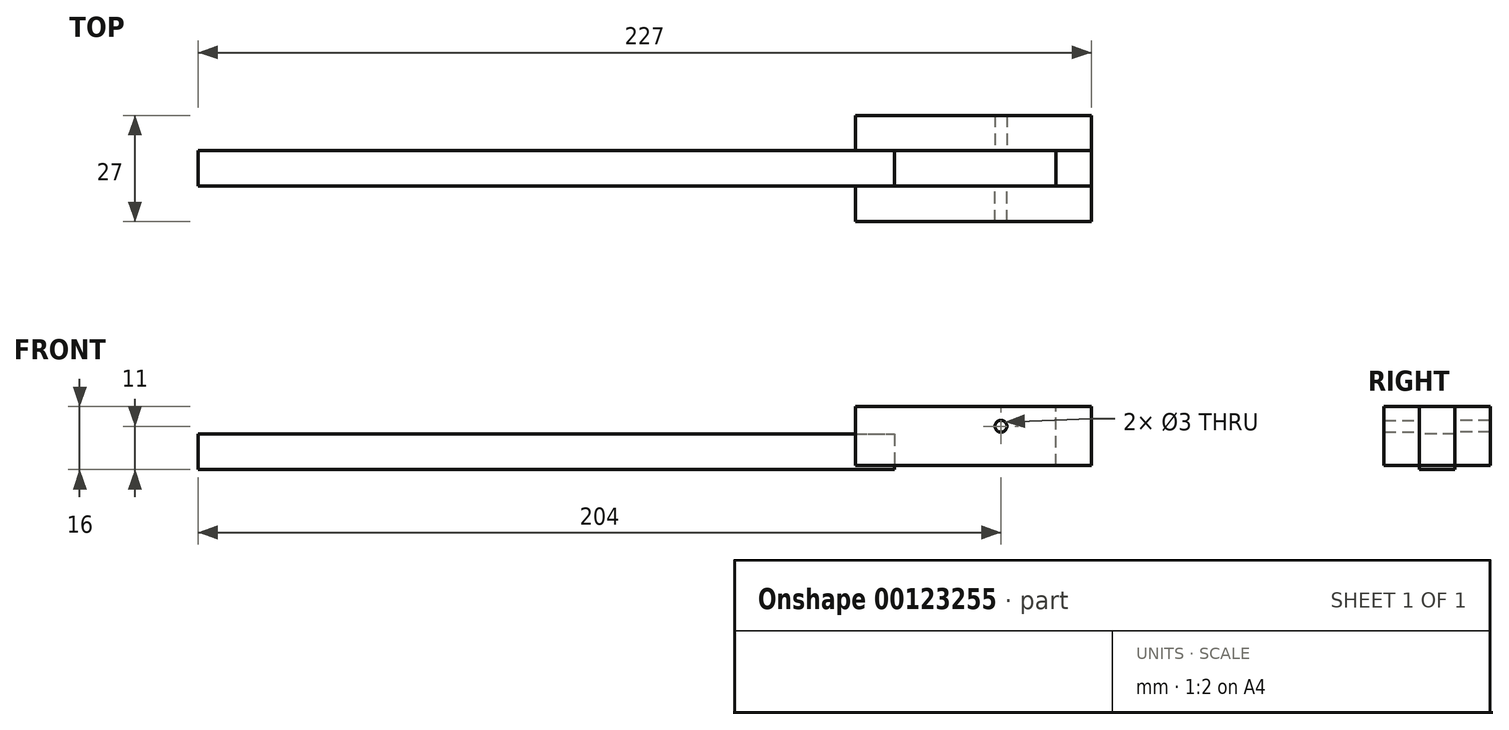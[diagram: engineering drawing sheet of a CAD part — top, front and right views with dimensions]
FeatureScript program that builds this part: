
annotation { "Feature Type Name" : "Feature", "Feature Type Description" : "" }
export const myFeature = defineFeature(function(context is Context, id is Id, definition is map)
    precondition{}
    {
        {
            var Q0;
            Q0=qCreatedBy(makeId("Front.planeOp"),FACE);
            var sketch = newSketch(context, id + "F0", { "sketchPlane" : qUnion([Q0])});
            skLineSegment(sketch, "E0.bottom", {"start": v(0, 9) * mm, "end": v(177, 9) * mm});
            skLineSegment(sketch, "E0.top", {"start": v(0, 0) * mm, "end": v(177, 0) * mm});
            skLineSegment(sketch, "E0.left", {"start": v(0, 9) * mm, "end": v(0, 0) * mm});
            skLineSegment(sketch, "E0.right", {"start": v(177, 9) * mm, "end": v(177, 0) * mm});
            skLineSegment(sketch, "E1.bottom", {"start": v(0, 0) * mm, "end": v(20, 0) * mm});
            skLineSegment(sketch, "E1.top", {"start": v(0, -30) * mm, "end": v(20, -30) * mm});
            skLineSegment(sketch, "E1.left", {"start": v(0, 0) * mm, "end": v(0, -30) * mm});
            skLineSegment(sketch, "E1.right", {"start": v(20, 0) * mm, "end": v(20, -30) * mm});
            skLineSegment(sketch, "E2.bottom", {"start": v(217.99, 1) * mm, "end": v(226.99, 1) * mm});
            skLineSegment(sketch, "E2.top", {"start": v(217.99, 16) * mm, "end": v(226.99, 16) * mm});
            skLineSegment(sketch, "E2.left", {"start": v(217.99, 1) * mm, "end": v(217.99, 16) * mm});
            skLineSegment(sketch, "E2.right", {"start": v(226.99, 1) * mm, "end": v(226.99, 16) * mm});
            skSolve(sketch);
        }
        {
            var Q0;
            Q0=makeQuery(id+"F0.imprint","IMPRINT",FACE,{"disambiguationData":[TD([[makeQuery(id+"F0.imprint","IMPRINT",EDGE,{"derivedFrom":sQuery(id+"F0.wireOp",EDGE,"E0.bottom")}),-1.0]])]});
            var Q1;
            Q1=makeQuery(id+"F0.imprint","IMPRINT",FACE,{"disambiguationData":[TD([[makeQuery(id+"F0.imprint","IMPRINT",EDGE,{"derivedFrom":sQuery(id+"F0.wireOp",EDGE,"E1.bottom")}),-1.0]])]});
            var Q2;
            Q2=makeQuery(id+"F0.imprint","IMPRINT",FACE,{"disambiguationData":[TD([[makeQuery(id+"F0.imprint","IMPRINT",EDGE,{"derivedFrom":sQuery(id+"F0.wireOp",EDGE,"E2.bottom")}),1.0]])]});
            extrude(context, id + "F1", {"entities" : qUnion([Q0, Q1, Q2]), "endBound" : BoundingType.SYMMETRIC, "depth" : 9 * mm});
        }
        {
            var Q0;
            Q0=qCreatedBy(makeId("Front.planeOp"),FACE);
            cPlane(context, id + "F2", {"entities" : qUnion([Q0]), "cplaneType" : CPlaneType.OFFSET, "offset" : 4.5 * mm, "oppositeDirection" : true, "width" : 150 * mm, "height" : 150 * mm});
        }
        {
            var Q0;
            Q0=qCreatedBy(id+"F2.planeOp",FACE);
            var sketch = newSketch(context, id + "F3", { "sketchPlane" : qUnion([Q0])});
            skLineSegment(sketch, "E3.bottom", {"start": v(167, 16) * mm, "end": v(227, 16) * mm});
            skLineSegment(sketch, "E3.top", {"start": v(167, 1) * mm, "end": v(227, 1) * mm});
            skLineSegment(sketch, "E3.left", {"start": v(167, 16) * mm, "end": v(167, 1) * mm});
            skLineSegment(sketch, "E3.right", {"start": v(227, 16) * mm, "end": v(227, 1) * mm});
            skCircle(sketch, "E4", {"center": v(204, 11) * mm, "radius": 1.5 * mm});
            skSolve(sketch);
        }
        {
            var Q0;
            Q0=makeQuery(id+"F3.imprint","IMPRINT",FACE,{"disambiguationData":[TD([[makeQuery(id+"F3.imprint","IMPRINT",EDGE,{"derivedFrom":sQuery(id+"F3.wireOp",EDGE,"E3.bottom")}),-1.0]])]});
            extrude(context, id + "F4", {"entities" : qUnion([Q0]), "operationType" : NewBodyOperationType.ADD, "oppositeDirection" : true, "depth" : 9 * mm});
        }
        {
            var Q0;
            Q0=makeQuery(id+"F1.opExtrude","SWEPT_BODY",BODY,{"disambiguationData":[OSD([sQuery(id+"F0.wireOp",EDGE,"E0.bottom"),sQuery(id+"F0.wireOp",EDGE,"E0.top"),sQuery(id+"F0.wireOp",EDGE,"E0.left"),sQuery(id+"F0.wireOp",EDGE,"E0.right"),sQuery(id+"F0.wireOp",EDGE,"E1.top"),sQuery(id+"F0.wireOp",EDGE,"E1.left"),sQuery(id+"F0.wireOp",EDGE,"E1.right")])]});
            var Q1;
            Q1=qCreatedBy(makeId("Front.planeOp"),FACE);
            mirror(context, id + "F5", {"entities" : qUnion([Q0]), "mirrorPlane" : qUnion([Q1])});
        }
    });
